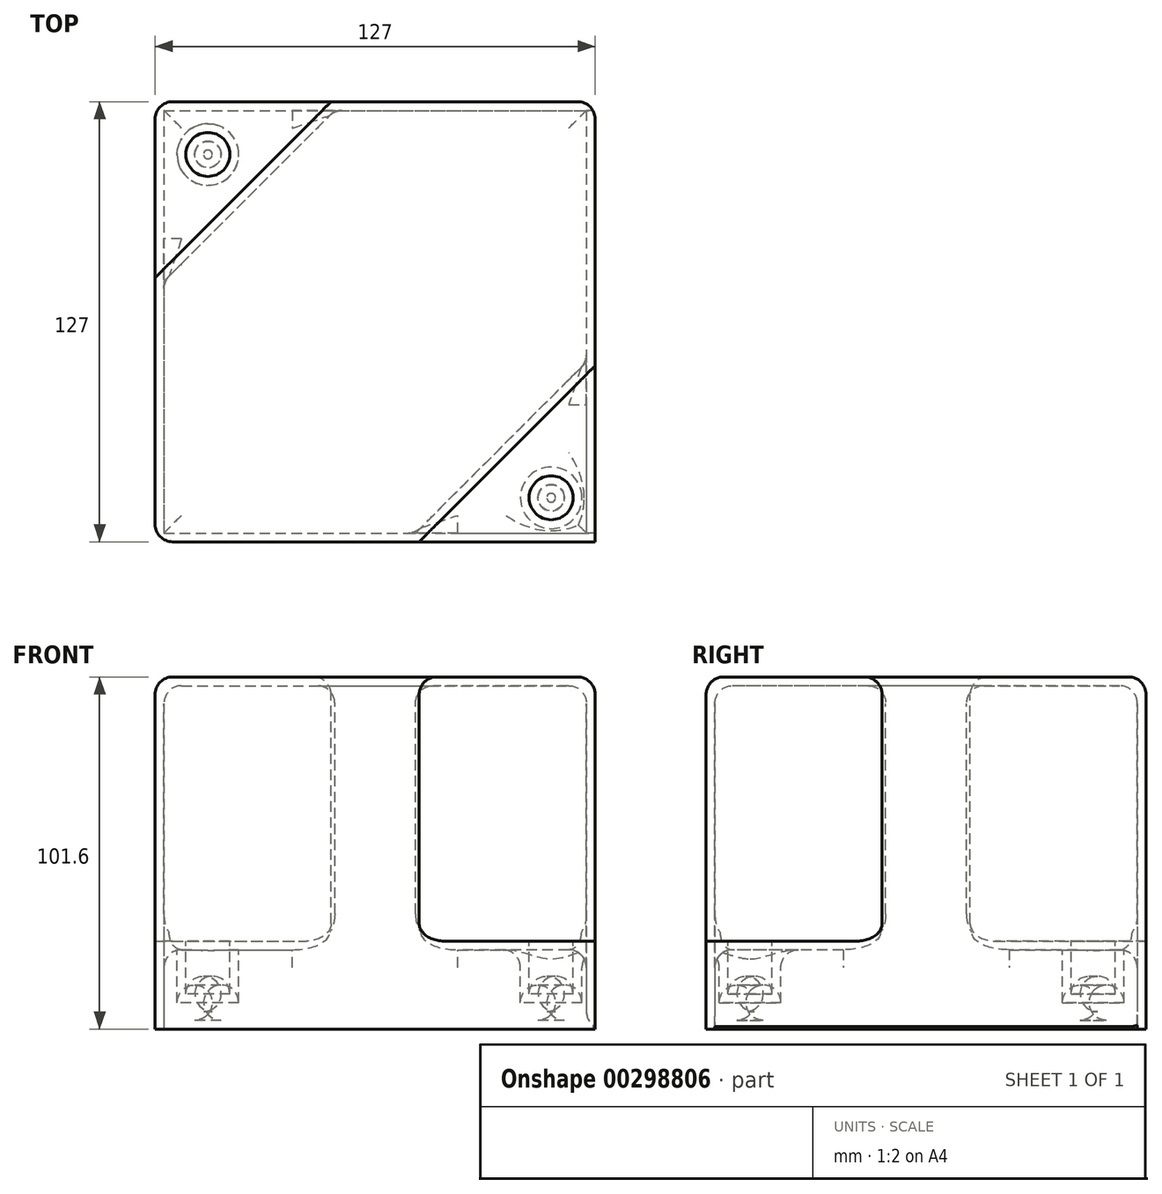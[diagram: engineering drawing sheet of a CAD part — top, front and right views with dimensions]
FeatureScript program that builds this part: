
annotation { "Feature Type Name" : "Feature", "Feature Type Description" : "" }
export const myFeature = defineFeature(function(context is Context, id is Id, definition is map)
    precondition{}
    {
        {
            var Q0;
            Q0=qCreatedBy(makeId("Top.planeOp"),FACE);
            var sketch = newSketch(context, id + "F0", { "sketchPlane" : qUnion([Q0])});
            skLineSegment(sketch, "E0.bottom", {"start": v(-63.5, 63.5) * mm, "end": v(63.5, 63.5) * mm});
            skLineSegment(sketch, "E0.top", {"start": v(-63.5, -63.5) * mm, "end": v(63.5, -63.5) * mm});
            skLineSegment(sketch, "E0.left", {"start": v(-63.5, 63.5) * mm, "end": v(-63.5, -63.5) * mm});
            skLineSegment(sketch, "E0.right", {"start": v(63.5, 63.5) * mm, "end": v(63.5, -63.5) * mm});
            skPoint(sketch, "E0.middle", {"position": v(0, 0) * mm});
            skSolve(sketch);
        }
        {
            var Q0;
            Q0=makeQuery(id+"F0.imprint","IMPRINT",FACE,{"disambiguationData":[TD([[makeQuery(id+"F0.imprint","IMPRINT",EDGE,{"derivedFrom":sQuery(id+"F0.wireOp",EDGE,"E0.bottom")}),-1.0]])]});
            extrude(context, id + "F1", {"entities" : qUnion([Q0]), "endBound" : BoundingType.SYMMETRIC, "depth" : 101.6 * mm});
        }
        {
            var Q0;
            Q0=makeQuery(id+"F1.opExtrude","CAP_FACE",FACE,{"disambiguationData":[OSD([sQuery(id+"F0.wireOp",EDGE,"E0.bottom"),sQuery(id+"F0.wireOp",EDGE,"E0.top"),sQuery(id+"F0.wireOp",EDGE,"E0.left"),sQuery(id+"F0.wireOp",EDGE,"E0.right")])],"isStart":false});
            var sketch = newSketch(context, id + "F2", { "sketchPlane" : qUnion([Q0])});
            skLineSegment(sketch, "E1", {"start": v(-63.5, 63.5) * mm, "end": v(-63.5, 12.7) * mm});
            skLineSegment(sketch, "E2", {"start": v(-63.5, 12.7) * mm, "end": v(-12.7, 63.5) * mm});
            skLineSegment(sketch, "E3", {"start": v(-12.7, 63.5) * mm, "end": v(-63.5, 63.5) * mm});
            skLineSegment(sketch, "E4", {"start": v(63.5, -63.5) * mm, "end": v(63.5, -12.7) * mm});
            skLineSegment(sketch, "E5", {"start": v(63.5, -12.7) * mm, "end": v(12.7, -63.5) * mm});
            skLineSegment(sketch, "E6", {"start": v(12.7, -63.5) * mm, "end": v(63.5, -63.5) * mm});
            skSolve(sketch);
        }
        {
            var Q0;
            Q0=makeQuery(id+"F2.imprint","IMPRINT",FACE,{"disambiguationData":[TD([[makeQuery(id+"F2.imprint","IMPRINT",EDGE,{"derivedFrom":sQuery(id+"F2.wireOp",EDGE,"E4")}),-1.0]])]});
            var Q1;
            Q1=makeQuery(id+"F2.imprint","IMPRINT",FACE,{"disambiguationData":[TD([[makeQuery(id+"F2.imprint","IMPRINT",EDGE,{"derivedFrom":sQuery(id+"F2.wireOp",EDGE,"E1")}),1.0]])]});
            extrude(context, id + "F3", {"entities" : qUnion([Q0, Q1]), "operationType" : NewBodyOperationType.REMOVE, "oppositeDirection" : true, "depth" : 76.2 * mm});
        }
        {
            var Q0;
            Q0=makeQuery(id+"F3.boolean.opBoolean","COPY",FACE,{"derivedFrom":makeQuery(id+"F3.opExtrude","CAP_FACE",FACE,{"disambiguationData":[OSD([sQuery(id+"F2.wireOp",EDGE,"E1"),sQuery(id+"F2.wireOp",EDGE,"E2"),sQuery(id+"F2.wireOp",EDGE,"E3")])],"isStart":false})});
            var sketch = newSketch(context, id + "F4", { "sketchPlane" : qUnion([Q0])});
            skCircle(sketch, "E7", {"center": v(-48.26, 48.26) * mm, "radius": 6.35 * mm});
            skSolve(sketch);
        }
        {
            var Q0;
            Q0=makeQuery(id+"F3.boolean.opBoolean","COPY",FACE,{"derivedFrom":makeQuery(id+"F3.opExtrude","CAP_FACE",FACE,{"disambiguationData":[OSD([sQuery(id+"F2.wireOp",EDGE,"E4"),sQuery(id+"F2.wireOp",EDGE,"E5"),sQuery(id+"F2.wireOp",EDGE,"E6")])],"isStart":false})});
            var sketch = newSketch(context, id + "F5", { "sketchPlane" : qUnion([Q0])});
            skCircle(sketch, "E8", {"center": v(50.8, -50.8) * mm, "radius": 6.35 * mm});
            skSolve(sketch);
        }
        {
            var Q0;
            Q0=makeQuery(id+"F5.imprint","IMPRINT",FACE,{"disambiguationData":[TD([[makeQuery(id+"F5.imprint","IMPRINT",EDGE,{"derivedFrom":sQuery(id+"F5.wireOp",EDGE,"E8")}),1.0]])]});
            var Q1;
            Q1=makeQuery(id+"F4.imprint","IMPRINT",FACE,{"disambiguationData":[TD([[makeQuery(id+"F4.imprint","IMPRINT",EDGE,{"derivedFrom":sQuery(id+"F4.wireOp",EDGE,"E7")}),1.0]])]});
            extrude(context, id + "F6", {"entities" : qUnion([Q0, Q1]), "operationType" : NewBodyOperationType.REMOVE, "oppositeDirection" : true, "depth" : 20.32 * mm});
        }
        {
            var Q0;
            Q0=makeQuery(id+"F1.opExtrude","CAP_FACE",FACE,{"disambiguationData":[OSD([sQuery(id+"F0.wireOp",EDGE,"E0.bottom"),sQuery(id+"F0.wireOp",EDGE,"E0.top"),sQuery(id+"F0.wireOp",EDGE,"E0.left"),sQuery(id+"F0.wireOp",EDGE,"E0.right")])],"isStart":true});
            shell(context, id + "F7", {"entities" : qUnion([Q0]), "thickness" : 2.54 * mm});
        }
        {
            var Q0;
            {var subQ0=sQuery(id+"F5.wireOp",EDGE,"E8");Q0=makeQuery(id+"F7.opShell","OFFSET_EDGE",EDGE,{"disambiguationData":[OSD([subQ0]),TDD([makeQuery(id+"F6.boolean.opBoolean","COPY",EDGE,{"derivedFrom":makeQuery(id+"F6.opExtrude","CAP_EDGE",EDGE,{"disambiguationData":[OSD([subQ0])],"isStart":false})})])]});}
            var Q1;
            {var subQ0=sQuery(id+"F5.wireOp",EDGE,"E8");Q1=makeQuery(id+"F7.opShell","OFFSET_EDGE",EDGE,{"disambiguationData":[OSD([subQ0]),TDD([makeQuery(id+"F6.boolean.opBoolean","COPY",EDGE,{"derivedFrom":makeQuery(id+"F6.opExtrude","CAP_EDGE",EDGE,{"disambiguationData":[OSD([subQ0])],"isStart":true})})])]});}
            var Q2;
            {var subQ0=sQuery(id+"F2.wireOp",EDGE,"E5");Q2=makeQuery(id+"F7.opShell","OFFSET_EDGE",EDGE,{"disambiguationData":[OSD([subQ0]),TDD([makeQuery(id+"F3.boolean.opBoolean","COPY",EDGE,{"derivedFrom":makeQuery(id+"F3.opExtrude","CAP_EDGE",EDGE,{"disambiguationData":[OSD([subQ0])],"isStart":false})})])]});}
            var Q3;
            Q3=makeQuery(id+"F7.opShell","OFFSET_EDGE",EDGE,{"disambiguationData":[OSD([sQuery(id+"F2.wireOp",EDGE,"E4")])]});
            var Q4;
            Q4=makeQuery(id+"F7.opShell","OFFSET_EDGE",EDGE,{"disambiguationData":[OSD([sQuery(id+"F2.wireOp",EDGE,"E6")])]});
            var Q5;
            Q5=makeQuery(id+"F7.opShell","OFFSET_EDGE",EDGE,{"disambiguationData":[OSD([sQuery(id+"F0.wireOp",EDGE,"E0.top"),sQuery(id+"F2.wireOp",EDGE,"E5"),sQuery(id+"F2.wireOp",EDGE,"E6")])]});
            var Q6;
            {var subQ0=sQuery(id+"F2.wireOp",EDGE,"E5");Q6=makeQuery(id+"F7.opShell","OFFSET_EDGE",EDGE,{"disambiguationData":[OSD([subQ0]),TDD([makeQuery(id+"F3.boolean.opBoolean","COPY",EDGE,{"derivedFrom":makeQuery(id+"F3.opExtrude","CAP_EDGE",EDGE,{"disambiguationData":[OSD([subQ0])],"isStart":true})})])]});}
            var Q7;
            {var subQ0=sQuery(id+"F0.wireOp",EDGE,"E0.bottom");Q7=makeQuery(id+"F7.opShell","OFFSET_EDGE",EDGE,{"disambiguationData":[OSD([subQ0]),TDD([makeQuery(id+"F1.opExtrude","CAP_EDGE",EDGE,{"disambiguationData":[OSD([subQ0])],"isStart":false})])]});}
            var Q8;
            {var subQ0=sQuery(id+"F2.wireOp",EDGE,"E2");Q8=makeQuery(id+"F7.opShell","OFFSET_EDGE",EDGE,{"disambiguationData":[OSD([subQ0]),TDD([makeQuery(id+"F3.boolean.opBoolean","COPY",EDGE,{"derivedFrom":makeQuery(id+"F3.opExtrude","CAP_EDGE",EDGE,{"disambiguationData":[OSD([subQ0])],"isStart":true})})])]});}
            var Q9;
            {var subQ0=sQuery(id+"F0.wireOp",EDGE,"E0.right");Q9=makeQuery(id+"F7.opShell","OFFSET_EDGE",EDGE,{"disambiguationData":[OSD([subQ0]),TDD([makeQuery(id+"F1.opExtrude","CAP_EDGE",EDGE,{"disambiguationData":[OSD([subQ0])],"isStart":false})])]});}
            var Q10;
            {var subQ0=sQuery(id+"F0.wireOp",EDGE,"E0.left");Q10=makeQuery(id+"F7.opShell","OFFSET_EDGE",EDGE,{"disambiguationData":[OSD([subQ0]),TDD([makeQuery(id+"F1.opExtrude","CAP_EDGE",EDGE,{"disambiguationData":[OSD([subQ0])],"isStart":false})])]});}
            var Q11;
            {var subQ0=sQuery(id+"F0.wireOp",EDGE,"E0.top");Q11=makeQuery(id+"F7.opShell","OFFSET_EDGE",EDGE,{"disambiguationData":[OSD([subQ0]),TDD([makeQuery(id+"F1.opExtrude","CAP_EDGE",EDGE,{"disambiguationData":[OSD([subQ0])],"isStart":false})])]});}
            var Q12;
            Q12=makeQuery(id+"F7.opShell","OFFSET_EDGE",EDGE,{"disambiguationData":[OSD([sQuery(id+"F0.wireOp",EDGE,"E0.bottom"),sQuery(id+"F2.wireOp",EDGE,"E2"),sQuery(id+"F2.wireOp",EDGE,"E3")])]});
            var Q13;
            Q13=makeQuery(id+"F7.opShell","OFFSET_EDGE",EDGE,{"disambiguationData":[OSD([sQuery(id+"F0.wireOp",EDGE,"E0.left"),sQuery(id+"F2.wireOp",EDGE,"E1"),sQuery(id+"F2.wireOp",EDGE,"E2")])]});
            var Q14;
            {var subQ0=sQuery(id+"F2.wireOp",EDGE,"E2");Q14=makeQuery(id+"F7.opShell","OFFSET_EDGE",EDGE,{"disambiguationData":[OSD([subQ0]),TDD([makeQuery(id+"F3.boolean.opBoolean","COPY",EDGE,{"derivedFrom":makeQuery(id+"F3.opExtrude","CAP_EDGE",EDGE,{"disambiguationData":[OSD([subQ0])],"isStart":false})})])]});}
            var Q15;
            {var subQ0=sQuery(id+"F4.wireOp",EDGE,"E7");Q15=makeQuery(id+"F7.opShell","OFFSET_EDGE",EDGE,{"disambiguationData":[OSD([subQ0]),TDD([makeQuery(id+"F6.boolean.opBoolean","COPY",EDGE,{"derivedFrom":makeQuery(id+"F6.opExtrude","CAP_EDGE",EDGE,{"disambiguationData":[OSD([subQ0])],"isStart":false})})])]});}
            var Q16;
            {var subQ0=sQuery(id+"F0.wireOp",EDGE,"E0.right");Q16=makeQuery(id+"F7.opShell","OFFSET_EDGE",EDGE,{"disambiguationData":[OSD([subQ0]),TDD([makeQuery(id+"F1.opExtrude","CAP_EDGE",EDGE,{"disambiguationData":[OSD([subQ0])],"isStart":true})])]});}
            var Q17;
            Q17=makeQuery(id+"F1.opExtrude","SWEPT_EDGE",EDGE,{"disambiguationData":[OSD([sQuery(id+"F0.wireOp",EDGE,"E0.bottom"),sQuery(id+"F0.wireOp",EDGE,"E0.left")])]});
            var Q18;
            Q18=makeQuery(id+"F3.boolean.opBoolean","COPY",EDGE,{"derivedFrom":makeQuery(id+"F3.opExtrude","CAP_EDGE",EDGE,{"disambiguationData":[OSD([sQuery(id+"F2.wireOp",EDGE,"E3")])],"isStart":false})});
            var Q19;
            Q19=makeQuery(id+"F3.boolean.opBoolean","COPY",EDGE,{"derivedFrom":makeQuery(id+"F3.opExtrude","CAP_EDGE",EDGE,{"disambiguationData":[OSD([sQuery(id+"F2.wireOp",EDGE,"E1")])],"isStart":false})});
            var Q20;
            Q20=makeQuery(id+"F3.boolean.opBoolean","COPY",EDGE,{"derivedFrom":makeQuery(id+"F3.opExtrude","CAP_EDGE",EDGE,{"disambiguationData":[OSD([sQuery(id+"F2.wireOp",EDGE,"E2")])],"isStart":false})});
            var Q21;
            Q21=makeQuery(id+"F3.boolean.opBoolean","COPY",EDGE,{"derivedFrom":makeQuery(id+"F3.opExtrude","CAP_EDGE",EDGE,{"disambiguationData":[OSD([sQuery(id+"F2.wireOp",EDGE,"E2")])],"isStart":true})});
            var Q22;
            Q22=makeQuery(id+"F6.boolean.opBoolean","COPY",EDGE,{"derivedFrom":makeQuery(id+"F6.opExtrude","CAP_EDGE",EDGE,{"disambiguationData":[OSD([sQuery(id+"F4.wireOp",EDGE,"E7")])],"isStart":false})});
            var Q23;
            Q23=makeQuery(id+"F1.opExtrude","SWEPT_EDGE",EDGE,{"disambiguationData":[OSD([sQuery(id+"F0.wireOp",EDGE,"E0.top"),sQuery(id+"F0.wireOp",EDGE,"E0.left")])]});
            var Q24;
            Q24=makeQuery(id+"F3.boolean.opBoolean","COPY",EDGE,{"derivedFrom":makeQuery(id+"F3.opExtrude","SWEPT_EDGE",EDGE,{"disambiguationData":[OSD([sQuery(id+"F0.wireOp",EDGE,"E0.right"),sQuery(id+"F2.wireOp",EDGE,"E4"),sQuery(id+"F2.wireOp",EDGE,"E5")])]})});
            var Q25;
            Q25=makeQuery(id+"F3.boolean.opBoolean","COPY",EDGE,{"derivedFrom":makeQuery(id+"F3.opExtrude","CAP_EDGE",EDGE,{"disambiguationData":[OSD([sQuery(id+"F2.wireOp",EDGE,"E4")])],"isStart":false})});
            var Q26;
            Q26=makeQuery(id+"F3.boolean.opBoolean","COPY",EDGE,{"derivedFrom":makeQuery(id+"F3.opExtrude","CAP_EDGE",EDGE,{"disambiguationData":[OSD([sQuery(id+"F2.wireOp",EDGE,"E6")])],"isStart":false})});
            var Q27;
            Q27=makeQuery(id+"F3.boolean.opBoolean","COPY",EDGE,{"derivedFrom":makeQuery(id+"F3.opExtrude","CAP_EDGE",EDGE,{"disambiguationData":[OSD([sQuery(id+"F2.wireOp",EDGE,"E5")])],"isStart":false})});
            var Q28;
            Q28=makeQuery(id+"F3.boolean.opBoolean","COPY",EDGE,{"derivedFrom":makeQuery(id+"F3.opExtrude","SWEPT_EDGE",EDGE,{"disambiguationData":[OSD([sQuery(id+"F0.wireOp",EDGE,"E0.top"),sQuery(id+"F2.wireOp",EDGE,"E5"),sQuery(id+"F2.wireOp",EDGE,"E6")])]})});
            var Q29;
            Q29=makeQuery(id+"F6.boolean.opBoolean","COPY",FACE,{"derivedFrom":makeQuery(id+"F6.opExtrude","CAP_FACE",FACE,{"disambiguationData":[OSD([sQuery(id+"F5.wireOp",EDGE,"E8")])],"isStart":false})});
            var Q30;
            Q30=makeQuery(id+"F1.opExtrude","SWEPT_EDGE",EDGE,{"disambiguationData":[OSD([sQuery(id+"F0.wireOp",EDGE,"E0.bottom"),sQuery(id+"F0.wireOp",EDGE,"E0.right")])]});
            var Q31;
            Q31=makeQuery(id+"F1.opExtrude","CAP_EDGE",EDGE,{"disambiguationData":[OSD([sQuery(id+"F0.wireOp",EDGE,"E0.right")])],"isStart":false});
            var Q32;
            Q32=makeQuery(id+"F1.opExtrude","CAP_EDGE",EDGE,{"disambiguationData":[OSD([sQuery(id+"F0.wireOp",EDGE,"E0.bottom")])],"isStart":false});
            var Q33;
            Q33=makeQuery(id+"F1.opExtrude","CAP_EDGE",EDGE,{"disambiguationData":[OSD([sQuery(id+"F0.wireOp",EDGE,"E0.left")])],"isStart":false});
            var Q34;
            Q34=makeQuery(id+"F1.opExtrude","CAP_EDGE",EDGE,{"disambiguationData":[OSD([sQuery(id+"F0.wireOp",EDGE,"E0.top")])],"isStart":false});
            var Q35;
            Q35=makeQuery(id+"F3.boolean.opBoolean","COPY",EDGE,{"derivedFrom":makeQuery(id+"F3.opExtrude","CAP_EDGE",EDGE,{"disambiguationData":[OSD([sQuery(id+"F2.wireOp",EDGE,"E5")])],"isStart":true})});
            fillet(context, id + "F8", {"entities" : qUnion([Q0, Q1, Q2, Q3, Q4, Q5, Q6, Q7, Q8, Q9, Q10, Q11, Q12, Q13, Q14, Q15, Q16, Q17, Q18, Q19, Q20, Q21, Q22, Q23, Q24, Q25, Q26, Q27, Q28, Q29, Q30, Q31, Q32, Q33, Q34, Q35]), "radius" : 5.08 * mm, "tangentPropagation" : true, "allowEdgeOverflow" : false});
        }
    });
